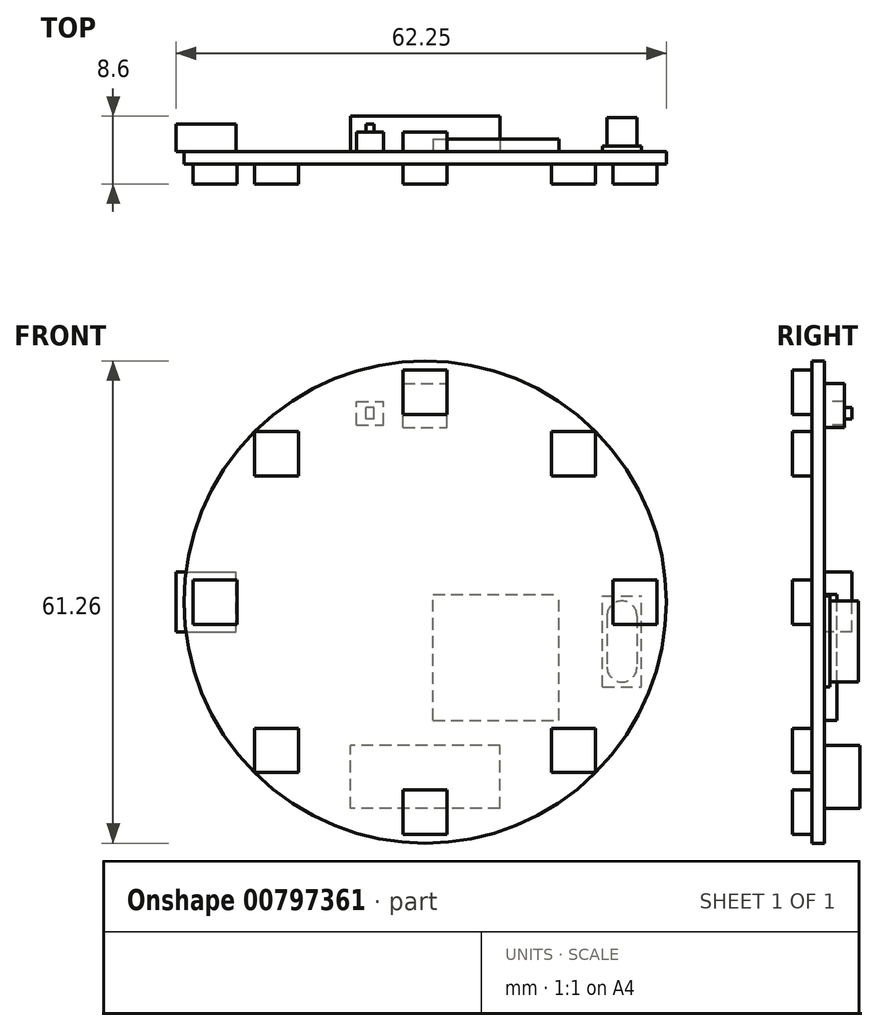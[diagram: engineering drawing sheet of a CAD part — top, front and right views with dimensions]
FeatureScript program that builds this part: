
annotation { "Feature Type Name" : "Feature", "Feature Type Description" : "" }
export const myFeature = defineFeature(function(context is Context, id is Id, definition is map)
    precondition{}
    {
        {
            var Q0;
            Q0=qCreatedBy(makeId("Front.planeOp"),FACE);
            var sketch = newSketch(context, id + "F0", { "sketchPlane" : qUnion([Q0])});
            skCircle(sketch, "E0", {"center": v(0, 0) * mm, "radius": 30.62 * mm});
            skSolve(sketch);
        }
        {
            var Q0;
            Q0 = qSketchRegion(id + "F0", true);
            extrude(context, id + "F1", {"entities" : qUnion([Q0]), "depth" : 1.6 * mm, "offsetDistance" : 25 * mm});
        }
        {
            var Q0;
            Q0=makeQuery(id+"F1.opExtrude","CAP_FACE",FACE,{"disambiguationData":[OSD([sQuery(id+"F0.wireOp",EDGE,"E0")])],"isStart":false});
            var sketch = newSketch(context, id + "F2", { "sketchPlane" : qUnion([Q0])});
            skCircle(sketch, "E1", {"center": v(0, 0) * mm, "radius": 26.67 * mm, "construction": true});
            skLineSegment(sketch, "E2.bottom", {"start": v(-23.87, -2.8) * mm, "end": v(-29.47, -2.8) * mm});
            skLineSegment(sketch, "E2.top", {"start": v(-23.87, 2.8) * mm, "end": v(-29.47, 2.8) * mm});
            skLineSegment(sketch, "E2.left", {"start": v(-23.87, -2.8) * mm, "end": v(-23.87, 2.8) * mm});
            skLineSegment(sketch, "E2.right", {"start": v(-29.47, -2.8) * mm, "end": v(-29.47, 2.8) * mm});
            skPoint(sketch, "E2.middle", {"position": v(-26.67, 0) * mm});
            skLineSegment(sketch, "E3.bottom", {"start": v(-16.06, 16.06) * mm, "end": v(-21.66, 16.06) * mm});
            skLineSegment(sketch, "E3.top", {"start": v(-16.06, 21.66) * mm, "end": v(-21.66, 21.66) * mm});
            skLineSegment(sketch, "E3.left", {"start": v(-16.06, 16.06) * mm, "end": v(-16.06, 21.66) * mm});
            skLineSegment(sketch, "E3.right", {"start": v(-21.66, 16.06) * mm, "end": v(-21.66, 21.66) * mm});
            skPoint(sketch, "E3.middle", {"position": v(-18.86, 18.86) * mm});
            skLineSegment(sketch, "E4.bottom", {"start": v(-2.8, 23.87) * mm, "end": v(2.8, 23.87) * mm});
            skLineSegment(sketch, "E4.top", {"start": v(-2.8, 29.47) * mm, "end": v(2.8, 29.47) * mm});
            skLineSegment(sketch, "E4.left", {"start": v(-2.8, 23.47) * mm, "end": v(-2.8, 29.47) * mm});
            skLineSegment(sketch, "E4.right", {"start": v(2.8, 23.87) * mm, "end": v(2.8, 29.47) * mm});
            skPoint(sketch, "E4.middle", {"position": v(0, 26.67) * mm});
            skLineSegment(sketch, "E5.bottom", {"start": v(16.06, 16.06) * mm, "end": v(21.66, 16.06) * mm});
            skLineSegment(sketch, "E5.top", {"start": v(16.06, 21.66) * mm, "end": v(21.66, 21.66) * mm});
            skLineSegment(sketch, "E5.left", {"start": v(16.06, 16.06) * mm, "end": v(16.06, 21.66) * mm});
            skLineSegment(sketch, "E5.right", {"start": v(21.66, 16.06) * mm, "end": v(21.66, 21.66) * mm});
            skPoint(sketch, "E5.middle", {"position": v(18.86, 18.86) * mm});
            skLineSegment(sketch, "E6.bottom", {"start": v(23.87, -2.8) * mm, "end": v(29.47, -2.8) * mm});
            skLineSegment(sketch, "E6.top", {"start": v(23.87, 2.8) * mm, "end": v(29.47, 2.8) * mm});
            skLineSegment(sketch, "E6.left", {"start": v(23.87, -2.8) * mm, "end": v(23.87, 2.8) * mm});
            skLineSegment(sketch, "E6.right", {"start": v(29.47, -2.8) * mm, "end": v(29.47, 2.8) * mm});
            skPoint(sketch, "E6.middle", {"position": v(26.67, 0) * mm});
            skLineSegment(sketch, "E7.bottom", {"start": v(16.06, -21.66) * mm, "end": v(21.66, -21.66) * mm});
            skLineSegment(sketch, "E7.top", {"start": v(16.06, -16.06) * mm, "end": v(21.66, -16.06) * mm});
            skLineSegment(sketch, "E7.left", {"start": v(16.06, -21.66) * mm, "end": v(16.06, -16.06) * mm});
            skLineSegment(sketch, "E7.right", {"start": v(21.66, -21.66) * mm, "end": v(21.66, -16.06) * mm});
            skPoint(sketch, "E7.middle", {"position": v(18.86, -18.86) * mm});
            skLineSegment(sketch, "E8.bottom", {"start": v(2.8, -29.47) * mm, "end": v(-2.8, -29.47) * mm});
            skLineSegment(sketch, "E8.top", {"start": v(2.8, -23.87) * mm, "end": v(-2.8, -23.87) * mm});
            skLineSegment(sketch, "E8.left", {"start": v(2.8, -29.47) * mm, "end": v(2.8, -23.87) * mm});
            skLineSegment(sketch, "E8.right", {"start": v(-2.8, -29.47) * mm, "end": v(-2.8, -23.87) * mm});
            skPoint(sketch, "E8.middle", {"position": v(0, -26.67) * mm});
            skLineSegment(sketch, "E9.bottom", {"start": v(-21.66, -21.66) * mm, "end": v(-16.06, -21.66) * mm});
            skLineSegment(sketch, "E9.top", {"start": v(-21.66, -16.06) * mm, "end": v(-16.06, -16.06) * mm});
            skLineSegment(sketch, "E9.left", {"start": v(-21.66, -21.66) * mm, "end": v(-21.66, -16.06) * mm});
            skLineSegment(sketch, "E9.right", {"start": v(-16.06, -21.66) * mm, "end": v(-16.06, -16.06) * mm});
            skPoint(sketch, "E9.middle", {"position": v(-18.86, -18.86) * mm});
            skLineSegment(sketch, "E10.bottom", {"start": v(-18.86, 18.86) * mm, "end": v(18.86, 18.86) * mm, "construction": true});
            skLineSegment(sketch, "E10.top", {"start": v(-18.86, -18.86) * mm, "end": v(18.86, -18.86) * mm, "construction": true});
            skLineSegment(sketch, "E10.left", {"start": v(-18.86, 18.86) * mm, "end": v(-18.86, -18.86) * mm, "construction": true});
            skLineSegment(sketch, "E10.right", {"start": v(18.86, 18.86) * mm, "end": v(18.86, -18.86) * mm, "construction": true});
            skSolve(sketch);
        }
        {
            var Q0;
            Q0 = qSketchRegion(id + "F2", true);
            extrude(context, id + "F3", {"entities" : qUnion([Q0]), "operationType" : NewBodyOperationType.ADD, "depth" : 2.5 * mm, "offsetDistance" : 25 * mm});
        }
        {
            var Q0;
            Q0=makeQuery(id+"F1.opExtrude","CAP_FACE",FACE,{"disambiguationData":[OSD([sQuery(id+"F0.wireOp",EDGE,"E0")])],"isStart":true});
            var sketch = newSketch(context, id + "F4", { "sketchPlane" : qUnion([Q0])});
            skLineSegment(sketch, "E11.bottom", {"start": v(2.8, 22.2) * mm, "end": v(-2.8, 22.2) * mm});
            skLineSegment(sketch, "E11.top", {"start": v(2.8, 27.8) * mm, "end": v(-2.8, 27.8) * mm});
            skLineSegment(sketch, "E11.left", {"start": v(2.8, 22.2) * mm, "end": v(2.8, 27.8) * mm});
            skLineSegment(sketch, "E11.right", {"start": v(-2.8, 22.2) * mm, "end": v(-2.8, 27.8) * mm});
            skPoint(sketch, "E11.middle", {"position": v(0, 25) * mm});
            skLineSegment(sketch, "E12.bottom", {"start": v(8.7, 22.5) * mm, "end": v(5.3, 22.5) * mm});
            skLineSegment(sketch, "E12.top", {"start": v(8.7, 25.5) * mm, "end": v(5.3, 25.5) * mm});
            skLineSegment(sketch, "E12.left", {"start": v(8.7, 22.5) * mm, "end": v(8.7, 25.5) * mm});
            skLineSegment(sketch, "E12.right", {"start": v(5.3, 22.5) * mm, "end": v(5.3, 25.5) * mm});
            skPoint(sketch, "E12.middle", {"position": v(7, 24) * mm});
            skLineSegment(sketch, "E13.bottom", {"start": v(31.62, -3.8) * mm, "end": v(24, -3.8) * mm});
            skLineSegment(sketch, "E13.top", {"start": v(31.62, 3.81) * mm, "end": v(24, 3.81) * mm});
            skLineSegment(sketch, "E13.left", {"start": v(31.62, -3.8) * mm, "end": v(31.62, 3.81) * mm});
            skLineSegment(sketch, "E13.right", {"start": v(24, -3.8) * mm, "end": v(24, 3.81) * mm});
            skPoint(sketch, "E13.middle", {"position": v(27.81, 0) * mm});
            skLineSegment(sketch, "E14.bottom", {"start": v(-9.5, -26.22) * mm, "end": v(9.5, -26.22) * mm});
            skLineSegment(sketch, "E14.top", {"start": v(-9.5, -18.23) * mm, "end": v(9.5, -18.23) * mm});
            skLineSegment(sketch, "E14.left", {"start": v(-9.5, -26.22) * mm, "end": v(-9.5, -18.23) * mm});
            skLineSegment(sketch, "E14.right", {"start": v(9.5, -26.22) * mm, "end": v(9.5, -18.23) * mm});
            skPoint(sketch, "E14.middle", {"position": v(0, -22.23) * mm});
            skLineSegment(sketch, "E15.bottom", {"start": v(-1, -15) * mm, "end": v(-17, -15) * mm});
            skLineSegment(sketch, "E15.top", {"start": v(-1, 1) * mm, "end": v(-17, 1) * mm});
            skLineSegment(sketch, "E15.left", {"start": v(-1, -15) * mm, "end": v(-1, 1) * mm});
            skLineSegment(sketch, "E15.right", {"start": v(-17, -15) * mm, "end": v(-17, 1) * mm});
            skPoint(sketch, "E15.middle", {"position": v(-9, -7) * mm});
            skArc(sketch, "E16", {"start": v(-23.1, -1.75) * mm, "mid": v(-25, 0.15) * mm, "end": v(-26.9, -1.75) * mm});
            skArc(sketch, "E17", {"start": v(-26.9, -8.25) * mm, "mid": v(-25, -10.15) * mm, "end": v(-23.1, -8.25) * mm});
            skLineSegment(sketch, "E18", {"start": v(-26.9, -1.75) * mm, "end": v(-26.9, -8.25) * mm});
            skLineSegment(sketch, "E19", {"start": v(-23.1, -1.75) * mm, "end": v(-23.1, -8.25) * mm});
            skLineSegment(sketch, "E20", {"start": v(-25, -1.75) * mm, "end": v(-25, -8.25) * mm, "construction": true});
            skPoint(sketch, "E21", {"position": v(-25, -5) * mm});
            skLineSegment(sketch, "E22.bottom", {"start": v(-22.55, -10.8) * mm, "end": v(-27.45, -10.8) * mm});
            skLineSegment(sketch, "E22.top", {"start": v(-22.55, 0.8) * mm, "end": v(-27.45, 0.8) * mm});
            skLineSegment(sketch, "E22.left", {"start": v(-22.55, -10.8) * mm, "end": v(-22.55, 0.8) * mm});
            skLineSegment(sketch, "E22.right", {"start": v(-27.45, -10.8) * mm, "end": v(-27.45, 0.8) * mm});
            skLineSegment(sketch, "E23.bottom", {"start": v(6.5, 23.3) * mm, "end": v(7.5, 23.3) * mm});
            skLineSegment(sketch, "E23.top", {"start": v(6.5, 24.7) * mm, "end": v(7.5, 24.7) * mm});
            skLineSegment(sketch, "E23.left", {"start": v(6.5, 23.3) * mm, "end": v(6.5, 24.7) * mm});
            skLineSegment(sketch, "E23.right", {"start": v(7.5, 23.3) * mm, "end": v(7.5, 24.7) * mm});
            skSolve(sketch);
        }
        {
            var Q0;
            Q0=makeQuery(id+"F4.imprint","IMPRINT",FACE,{"disambiguationData":[TD([[makeQuery(id+"F4.imprint","IMPRINT",EDGE,{"derivedFrom":sQuery(id+"F4.wireOp",EDGE,"E15.bottom")}),-1.0]])]});
            extrude(context, id + "F5", {"entities" : qUnion([Q0]), "operationType" : NewBodyOperationType.ADD, "depth" : 1.6 * mm, "offsetDistance" : 25 * mm});
        }
        {
            var Q0;
            Q0=makeQuery(id+"F4.imprint","IMPRINT",FACE,{"disambiguationData":[TD([[makeQuery(id+"F4.imprint","IMPRINT",EDGE,{"derivedFrom":sQuery(id+"F4.wireOp",EDGE,"E11.bottom")}),-1.0]])]});
            var Q1;
            Q1=sQuery(id+"F4.wireOp",EDGE,"E11.bottom");
            var Q2;
            Q2=sQuery(id+"F4.wireOp",EDGE,"E11.top");
            var Q3;
            Q3=sQuery(id+"F4.wireOp",EDGE,"E11.right");
            var Q4;
            Q4=sQuery(id+"F4.wireOp",EDGE,"E11.left");
            extrude(context, id + "F6", {"entities" : qUnion([Q0]), "operationType" : NewBodyOperationType.ADD, "surfaceEntities" : qUnion([Q1, Q2, Q3, Q4]), "depth" : 2.5 * mm, "offsetDistance" : 25 * mm});
        }
        {
            var Q0;
            Q0=makeQuery(id+"F4.imprint","IMPRINT",FACE,{"disambiguationData":[TD([[makeQuery(id+"F4.imprint","IMPRINT",EDGE,{"derivedFrom":sQuery(id+"F4.wireOp",EDGE,"E12.bottom")}),-1.0]])]});
            extrude(context, id + "F7", {"entities" : qUnion([Q0]), "operationType" : NewBodyOperationType.ADD, "depth" : 2.5 * mm, "offsetDistance" : 25 * mm});
        }
        {
            var Q0;
            Q0=makeQuery(id+"F4.imprint","IMPRINT",FACE,{"disambiguationData":[TD([[makeQuery(id+"F4.imprint","IMPRINT",EDGE,{"derivedFrom":sQuery(id+"F4.wireOp",EDGE,"E23.bottom")}),1.0]])]});
            extrude(context, id + "F8", {"entities" : qUnion([Q0]), "operationType" : NewBodyOperationType.ADD, "depth" : 3.5 * mm, "offsetDistance" : 25 * mm});
        }
        {
            var Q0;
            Q0=sQuery(id+"F4.wireOp",EDGE,"E23.bottom");
            var Q1;
            Q1=sQuery(id+"F4.wireOp",EDGE,"E23.left");
            var Q2;
            Q2=sQuery(id+"F4.wireOp",EDGE,"E23.top");
            var Q3;
            Q3=sQuery(id+"F4.wireOp",EDGE,"E23.right");
            extrude(context, id + "F9", {"bodyType" : ToolBodyType.SURFACE, "operationType" : NewBodyOperationType.ADD, "surfaceEntities" : qUnion([Q0, Q1, Q2, Q3]), "depth" : 3.8 * mm, "offsetDistance" : 25 * mm});
        }
        {
            var Q0;
            Q0=makeQuery(id+"F4.imprint","IMPRINT",FACE,{"disambiguationData":[TD([[makeQuery(id+"F4.imprint","IMPRINT",EDGE,{"derivedFrom":sQuery(id+"F4.wireOp",EDGE,"E14.bottom")}),1.0]])]});
            extrude(context, id + "F10", {"entities" : qUnion([Q0]), "operationType" : NewBodyOperationType.ADD, "depth" : 4.5 * mm, "offsetDistance" : 25 * mm});
        }
        {
            var Q0;
            Q0=makeQuery(id+"F4.imprint","IMPRINT",FACE,{"disambiguationData":[TD([[makeQuery(id+"F4.imprint","IMPRINT",EDGE,{"derivedFrom":sQuery(id+"F4.wireOp",EDGE,"E16")}),-1.0]])]});
            extrude(context, id + "F11", {"entities" : qUnion([Q0]), "operationType" : NewBodyOperationType.ADD, "depth" : .7 * mm, "offsetDistance" : 25 * mm});
        }
        {
            var Q0;
            Q0=makeQuery(id+"F4.imprint","IMPRINT",FACE,{"disambiguationData":[TD([[makeQuery(id+"F4.imprint","IMPRINT",EDGE,{"derivedFrom":sQuery(id+"F4.wireOp",EDGE,"E16")}),1.0]])]});
            extrude(context, id + "F12", {"entities" : qUnion([Q0]), "operationType" : NewBodyOperationType.ADD, "depth" : 4.3 * mm, "offsetDistance" : 25 * mm});
        }
        {
            var Q0;
            {var subQ0=sQuery(id+"F4.wireOp",EDGE,"E13.right");Q0=makeQuery(id+"F4.imprint","IMPRINT",FACE,{"disambiguationData":[TD([[makeQuery(id+"F4.imprint","IMPRINT",EDGE,{"derivedFrom":subQ0}),-1.0]])]});}
            var Q1;
            {var subQ0=sQuery(id+"F4.wireOp",EDGE,"E13.left");Q1=makeQuery(id+"F4.imprint","IMPRINT",FACE,{"disambiguationData":[TD([[makeQuery(id+"F4.imprint","IMPRINT",EDGE,{"derivedFrom":subQ0}),1.0]])]});}
            extrude(context, id + "F13", {"entities" : qUnion([Q0, Q1]), "operationType" : NewBodyOperationType.ADD, "depth" : 3.5 * mm, "offsetDistance" : 25 * mm});
        }
    });
